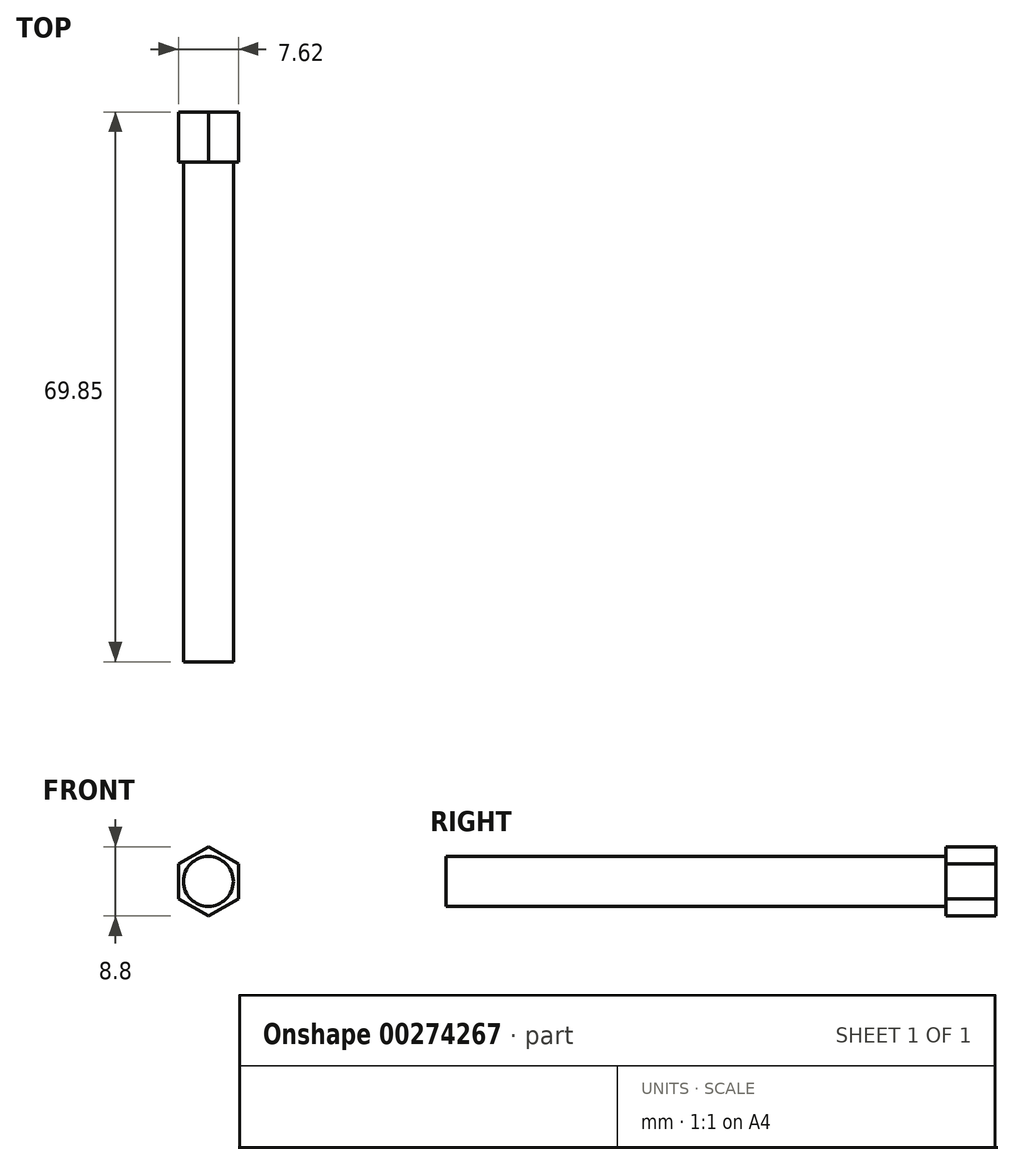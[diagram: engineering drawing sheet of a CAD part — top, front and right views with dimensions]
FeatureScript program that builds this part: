
annotation { "Feature Type Name" : "Feature", "Feature Type Description" : "" }
export const myFeature = defineFeature(function(context is Context, id is Id, definition is map)
    precondition{}
    {
        {
            var Q0;
            Q0=qCreatedBy(makeId("Front.planeOp"),FACE);
            var sketch = newSketch(context, id + "F0", { "sketchPlane" : qUnion([Q0])});
            skCircle(sketch, "E0", {"center": v(0, 0) * mm, "radius": 3.18 * mm});
            skCircle(sketch, "E1.cCircle", {"center": v(0, 0) * mm, "radius": 3.81 * mm, "construction": true});
            skLineSegment(sketch, "E1.0", {"start": v(-3.81, -2.2) * mm, "end": v(-3.81, 2.2) * mm});
            skLineSegment(sketch, "E1.1", {"start": v(-3.81, 2.2) * mm, "end": v(0, 4.4) * mm});
            skLineSegment(sketch, "E1.2", {"start": v(0, 4.4) * mm, "end": v(3.8, 2.2) * mm});
            skLineSegment(sketch, "E1.3", {"start": v(3.8, 2.2) * mm, "end": v(3.81, -2.2) * mm});
            skLineSegment(sketch, "E1.4", {"start": v(3.8, -2.2) * mm, "end": v(0, -4.4) * mm});
            skLineSegment(sketch, "E1.5", {"start": v(0, -4.4) * mm, "end": v(-3.81, -2.2) * mm});
            skPoint(sketch, "E1.0.midPoint", {"position": v(-3.81, 0) * mm});
            skSolve(sketch);
        }
        {
            var Q0;
            Q0=makeQuery(id+"F0.imprint","IMPRINT",FACE,{"disambiguationData":[TD([[makeQuery(id+"F0.imprint","IMPRINT",EDGE,{"derivedFrom":sQuery(id+"F0.wireOp",EDGE,"E0")}),1.0]])]});
            extrude(context, id + "F1", {"entities" : qUnion([Q0]), "depth" : 63.5 * mm});
        }
        {
            var Q0;
            Q0 = qSketchRegion(id + "F0", true);
            var Q1;
            Q1=makeQuery(id+"F1.opExtrude","CAP_FACE",FACE,{"disambiguationData":[OSD([sQuery(id+"F0.wireOp",EDGE,"E0")])],"isStart":true});
            extrude(context, id + "F2", {"entities" : qUnion([Q0, Q1]), "operationType" : NewBodyOperationType.ADD, "oppositeDirection" : true, "depth" : 6.35 * mm});
        }
    });
